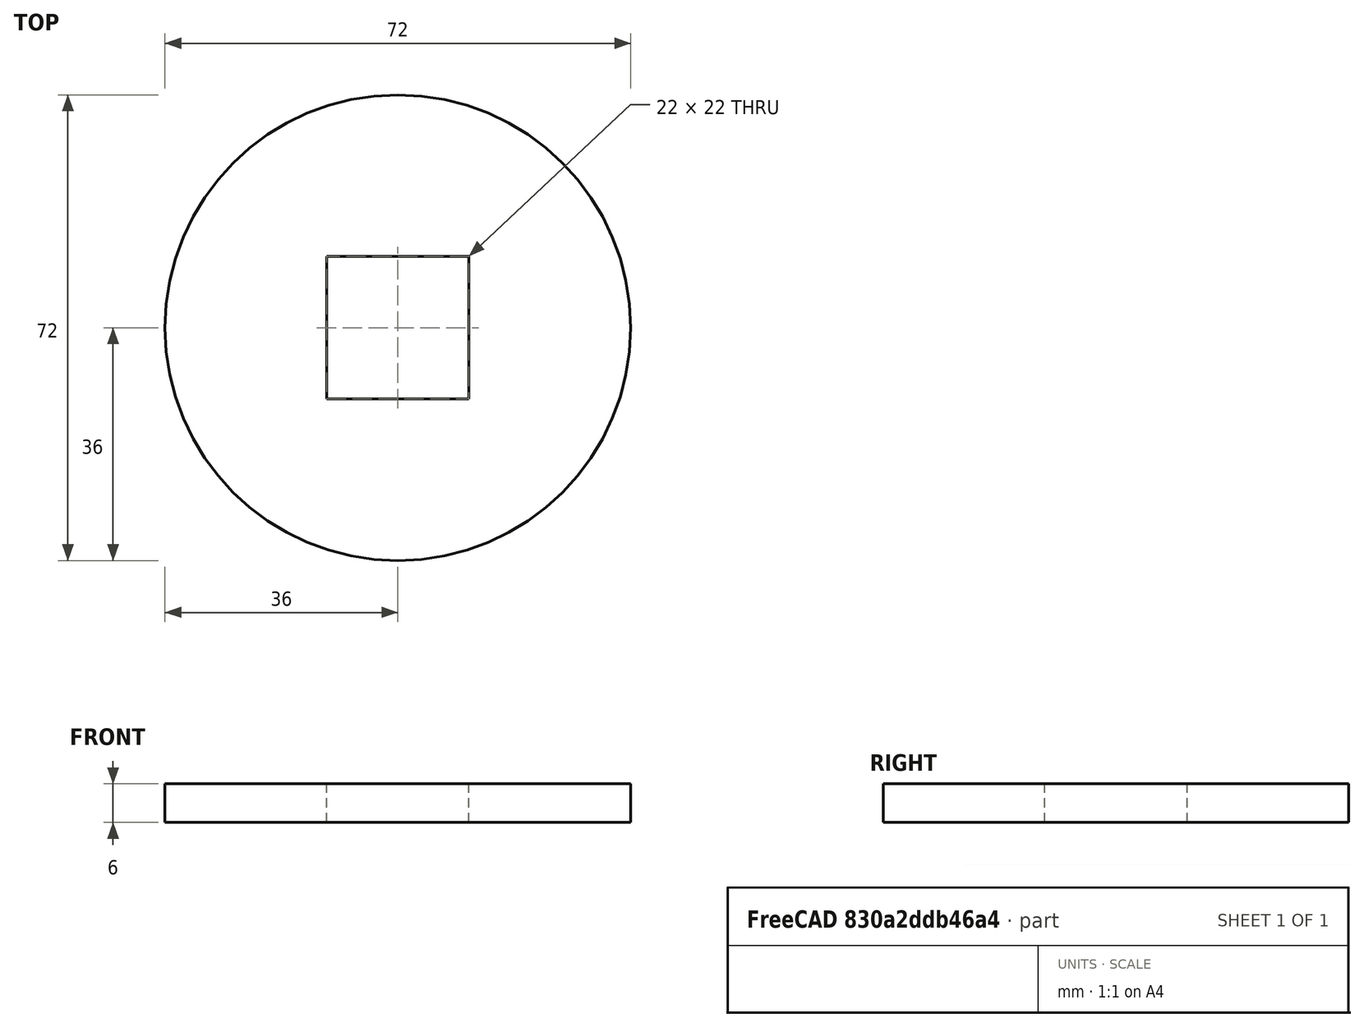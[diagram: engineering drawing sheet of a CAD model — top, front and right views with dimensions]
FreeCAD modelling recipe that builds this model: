
FCSTD DOCUMENT  (FreeCAD 0.15R4671 (Git))
Label: DIN440_CLASS_V_M20
License: CreativeCommons Attribution-ShareAlike
LicenseURL: http://creativecommons.org/licenses/by-sa/4.0/
objects: Sketcher::SketchObject×1, PartDesign::Pad×1
note: 3 computed .brp shape members not serialized (recipe doc carries the construction recipe); baked Part::Feature solids carry a one-line shape summary decoded from their .brp

FEATURE [Sketcher::SketchObject] Sketch
  sketch-geometry (5):
    g0: Circle CenterX=0 CenterY=0 CenterZ=0 NormalX=0 NormalY=0 NormalZ=1 Radius=36
    g1: LineSegment StartX=-11 StartY=11 StartZ=0 EndX=11 EndY=11 EndZ=0
    g2: LineSegment StartX=11 StartY=11 StartZ=0 EndX=11 EndY=-11 EndZ=0
    g3: LineSegment StartX=11 StartY=-11 StartZ=0 EndX=-11 EndY=-11 EndZ=0
    g4: LineSegment StartX=-11 StartY=-11 StartZ=0 EndX=-11 EndY=11 EndZ=0
  constraints (15):
    c: Coincident(g0,g-1)
    c: Radius(g0) = 36
    c: Coincident(g1,g2)
    c: Coincident(g2,g3)
    c: Coincident(g3,g4)
    c: Coincident(g4,g1)
    c: Horizontal(g1)
    c: Horizontal(g3)
    c: Vertical(g2)
    c: Vertical(g4)
    c: Equal(g1,g4)
    c: Equal(g4,g3)
    c: Equal(g3,g2)
    c: DistanceX(g1,g1) = 22
    c: Symmetric(g2,g1,g-1)
FEATURE [PartDesign::Pad] Pad
  Length = 6
  Length2 = 100
  Sketch = -> Sketch
  Type = 0
